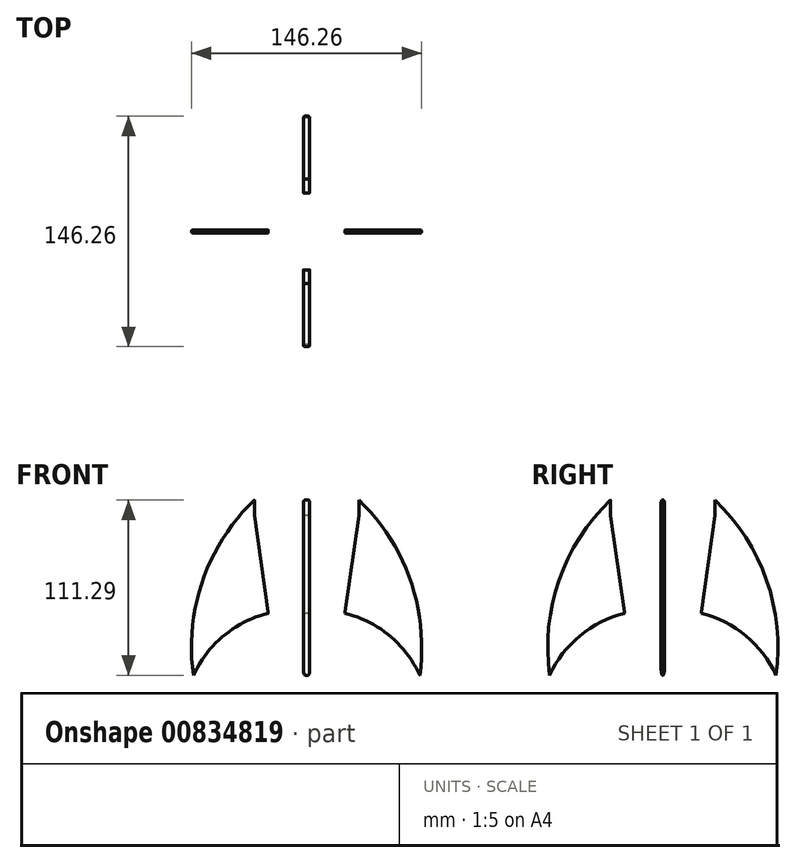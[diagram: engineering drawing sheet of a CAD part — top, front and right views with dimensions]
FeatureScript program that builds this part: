
annotation { "Feature Type Name" : "Feature", "Feature Type Description" : "" }
export const myFeature = defineFeature(function(context is Context, id is Id, definition is map)
    precondition{}
    {
        {
            var Q0;
            Q0=qCreatedBy(makeId("Front.planeOp"),FACE);
            var sketch = newSketch(context, id + "F0", { "sketchPlane" : qUnion([Q0])});
            skLineSegment(sketch, "E0", {"start": v(0, 1.98) * mm, "end": v(0, 124.8) * mm, "construction": true});
            skLineSegment(sketch, "E1.bottom", {"start": v(-9, 31.24) * mm, "end": v(9, 31.24) * mm, "construction": true});
            skLineSegment(sketch, "E1.top", {"start": v(-9, 101.24) * mm, "end": v(9, 101.24) * mm, "construction": true});
            skLineSegment(sketch, "E1.left", {"start": v(-9, 31.24) * mm, "end": v(-9, 101.24) * mm, "construction": true});
            skLineSegment(sketch, "E1.right", {"start": v(9, 31.24) * mm, "end": v(9, 101.24) * mm, "construction": true});
            skSolve(sketch);
        }
        {
            var Q0;
            Q0=qCreatedBy(makeId("Front.planeOp"),FACE);
            var sketch = newSketch(context, id + "F1", { "sketchPlane" : qUnion([Q0])});
            skLineSegment(sketch, "E2.MirrorCS", {"start": v(9.15, 101.26) * mm, "end": v(9.15, 33.17) * mm});
            skLineSegment(sketch, "E3.MirrorCS", {"start": v(33.01, 101.3) * mm, "end": v(23.86, 34.74) * mm});
            skLineSegment(sketch, "E4.MirrorCS", {"start": v(32, 101.3) * mm, "end": v(9.15, 101.26) * mm});
            skLineSegment(sketch, "E5.MirrorCS", {"start": v(32, 101.3) * mm, "end": v(32, 111.3) * mm});
            skLineSegment(sketch, "E6.MirrorCS", {"start": v(33.01, 111.3) * mm, "end": v(33.01, 101.3) * mm});
            skLineSegment(sketch, "E7.MirrorCS", {"start": v(32, 111.3) * mm, "end": v(33.01, 111.3) * mm});
            skLineSegment(sketch, "E8.MirrorCS", {"start": v(19.69, 21.09) * mm, "end": v(19.69, 34.74) * mm});
            skLineSegment(sketch, "E9.MirrorCS", {"start": v(19.69, 34.74) * mm, "end": v(23.86, 34.74) * mm});
            skLineSegment(sketch, "E10.MirrorCS", {"start": v(9.15, 33.17) * mm, "end": v(11.05, 33.17) * mm});
            skLineSegment(sketch, "E11.MirrorCS", {"start": v(11.05, 33.17) * mm, "end": v(11.05, 30.73) * mm});
            skLineSegment(sketch, "E12.MirrorCS", {"start": v(11.05, 30.73) * mm, "end": v(18.59, 21.09) * mm});
            skLineSegment(sketch, "E13.MirrorCS", {"start": v(18.59, 21.09) * mm, "end": v(19.69, 21.09) * mm});
            skLineSegment(sketch, "E14", {"start": v(12.5, 94.18) * mm, "end": v(28.58, 94.18) * mm});
            skLineSegment(sketch, "E15", {"start": v(28.58, 94.18) * mm, "end": v(21.03, 39.29) * mm});
            skLineSegment(sketch, "E16", {"start": v(21.03, 39.29) * mm, "end": v(12.3, 39.29) * mm});
            skLineSegment(sketch, "E17", {"start": v(12.3, 39.29) * mm, "end": v(12.5, 94.18) * mm});
            skSolve(sketch);
        }
        {
            var Q0;
            Q0=sQuery(id+"F1.wireOp",EDGE,"E2.MirrorCS");
            var Q1;
            Q1=sQuery(id+"F1.wireOp",EDGE,"E4.MirrorCS");
            var Q2;
            Q2=sQuery(id+"F1.wireOp",EDGE,"E6.MirrorCS");
            var Q3;
            Q3=sQuery(id+"F1.wireOp",EDGE,"E3.MirrorCS");
            var Q4;
            Q4=sQuery(id+"F1.wireOp",EDGE,"E5.MirrorCS");
            var Q5;
            Q5=sQuery(id+"F1.wireOp",EDGE,"E9.MirrorCS");
            var Q6;
            Q6=sQuery(id+"F1.wireOp",EDGE,"E11.MirrorCS");
            var Q7;
            Q7=sQuery(id+"F1.wireOp",EDGE,"E7.MirrorCS");
            var Q8;
            Q8=sQuery(id+"F1.wireOp",EDGE,"E10.MirrorCS");
            var Q9;
            Q9=sQuery(id+"F1.wireOp",EDGE,"E8.MirrorCS");
            var Q10;
            Q10=sQuery(id+"F1.wireOp",EDGE,"E12.MirrorCS");
            var Q11;
            Q11=sQuery(id+"F1.wireOp",EDGE,"E13.MirrorCS");
            var Q12;
            Q12=sQuery(id+"F0.wireOp",EDGE,"E0");
            revolve(context, id + "F2", {"bodyType" : ToolBodyType.SURFACE, "surfaceOperationType" : NewSurfaceOperationType.NEW, "surfaceEntities" : qUnion([Q0, Q1, Q2, Q3, Q4, Q5, Q6, Q7, Q8, Q9, Q10, Q11]), "axis" : qUnion([Q12]), "revolveType" : RevolveType.FULL});
        }
        {
            var Q0;
            Q0=makeQuery(id+"F2.opRevolve","SWEPT_EDGE",EDGE,{"disambiguationData":[OSD([sQuery(id+"F1.wireOp",VERTEX,"E4.MirrorCS.end")])]});
            var Q1;
            Q1=makeQuery(id+"F2.opRevolve","SWEPT_EDGE",EDGE,{"disambiguationData":[OSD([sQuery(id+"F1.wireOp",VERTEX,"E13.MirrorCS.end")])]});
            var Q2;
            Q2=makeQuery(id+"F2.opRevolve","SWEPT_EDGE",EDGE,{"disambiguationData":[OSD([sQuery(id+"F1.wireOp",VERTEX,"E10.MirrorCS.start")])]});
            fillet(context, id + "F3", {"entities" : qUnion([Q0, Q1, Q2]), "radius" : 5 * mm, "tangentPropagation" : true, "allowEdgeOverflow" : false});
        }
        {
            var Q0;
            Q0=qCreatedBy(makeId("Front.planeOp"),FACE);
            var sketch = newSketch(context, id + "F4", { "sketchPlane" : qUnion([Q0])});
            skArc(sketch, "E18", {"start": v(-24.4, 39.36) * mm, "mid": v(-52.64, 25.1) * mm, "end": v(-71.9, 0) * mm});
            skArc(sketch, "E19", {"start": v(-33.16, 111.3) * mm, "mid": v(-65.94, 60.31) * mm, "end": v(-71.9, 0) * mm});
            skLineSegment(sketch, "E20", {"start": v(-33.16, 111.3) * mm, "end": v(-33.16, 101.44) * mm});
            skLineSegment(sketch, "E21", {"start": v(-33.16, 101.44) * mm, "end": v(-24.4, 39.36) * mm});
            skArc(sketch, "E22.MirrorCS", {"start": v(33.16, 111.3) * mm, "mid": v(65.94, 60.31) * mm, "end": v(71.9, 0) * mm});
            skArc(sketch, "E23.MirrorCS", {"start": v(24.4, 39.36) * mm, "mid": v(52.64, 25.1) * mm, "end": v(71.9, 0) * mm});
            skLineSegment(sketch, "E24.MirrorCS", {"start": v(33.16, 101.44) * mm, "end": v(24.4, 39.36) * mm});
            skLineSegment(sketch, "E25.MirrorCS", {"start": v(33.16, 111.3) * mm, "end": v(33.16, 101.44) * mm});
            skSolve(sketch);
        }
        {
            var Q0;
            Q0 = qSketchRegion(id + "F4", true);
            extrude(context, id + "F5", {"entities" : qUnion([Q0]), "depth" : 1 * mm, "offsetDistance" : 25 * mm, "hasSecondDirection" : true, "secondDirectionOppositeDirection" : true, "secondDirectionDepth" : 1 * mm});
        }
        {
            var Q0;
            Q0=qCreatedBy(makeId("Right.planeOp"),FACE);
            var sketch = newSketch(context, id + "F6", { "sketchPlane" : qUnion([Q0])});
            skArc(sketch, "E26", {"start": v(-24.36, 39.36) * mm, "mid": v(-52.6, 25.1) * mm, "end": v(-71.86, 0) * mm});
            skArc(sketch, "E27", {"start": v(-33.12, 111.3) * mm, "mid": v(-65.9, 60.31) * mm, "end": v(-71.86, 0) * mm});
            skLineSegment(sketch, "E28", {"start": v(-33.12, 111.3) * mm, "end": v(-33.12, 101.44) * mm});
            skLineSegment(sketch, "E29", {"start": v(-33.12, 101.44) * mm, "end": v(-24.36, 39.36) * mm});
            skArc(sketch, "E30.MirrorCS", {"start": v(33.2, 111.3) * mm, "mid": v(65.98, 60.31) * mm, "end": v(71.94, 0) * mm});
            skArc(sketch, "E31.MirrorCS", {"start": v(24.44, 39.36) * mm, "mid": v(52.69, 25.1) * mm, "end": v(71.94, 0) * mm});
            skLineSegment(sketch, "E32.MirrorCS", {"start": v(33.2, 101.44) * mm, "end": v(24.44, 39.36) * mm});
            skLineSegment(sketch, "E33.MirrorCS", {"start": v(33.2, 111.3) * mm, "end": v(33.2, 101.44) * mm});
            skSolve(sketch);
        }
        {
            var Q0;
            Q0 = qSketchRegion(id + "F6", true);
            extrude(context, id + "F7", {"entities" : qUnion([Q0]), "depth" : 2 * mm, "offsetDistance" : 25 * mm, "hasSecondDirection" : true, "secondDirectionOppositeDirection" : true, "secondDirectionDepth" : 2 * mm});
        }
        {
            var Q0;
            Q0=makeQuery(id+"F7.opExtrude","CAP_EDGE",EDGE,{"disambiguationData":[OSD([sQuery(id+"F6.wireOp",EDGE,"E27")])],"isStart":true});
            var Q1;
            Q1=makeQuery(id+"F7.opExtrude","CAP_EDGE",EDGE,{"disambiguationData":[OSD([sQuery(id+"F6.wireOp",EDGE,"E26")])],"isStart":true});
            var Q2;
            Q2=makeQuery(id+"F7.opExtrude","CAP_EDGE",EDGE,{"disambiguationData":[OSD([sQuery(id+"F6.wireOp",EDGE,"E26")])],"isStart":false});
            var Q3;
            Q3=makeQuery(id+"F5.opExtrude","CAP_EDGE",EDGE,{"disambiguationData":[OSD([sQuery(id+"F4.wireOp",EDGE,"E23.MirrorCS")])],"isStart":false});
            var Q4;
            Q4=makeQuery(id+"F5.opExtrude","CAP_EDGE",EDGE,{"disambiguationData":[OSD([sQuery(id+"F4.wireOp",EDGE,"E23.MirrorCS")])],"isStart":true});
            var Q5;
            Q5=makeQuery(id+"F7.opExtrude","CAP_EDGE",EDGE,{"disambiguationData":[OSD([sQuery(id+"F6.wireOp",EDGE,"E31.MirrorCS")])],"isStart":false});
            var Q6;
            Q6=makeQuery(id+"F7.opExtrude","CAP_EDGE",EDGE,{"disambiguationData":[OSD([sQuery(id+"F6.wireOp",EDGE,"E31.MirrorCS")])],"isStart":true});
            var Q7;
            Q7=makeQuery(id+"F5.opExtrude","CAP_EDGE",EDGE,{"disambiguationData":[OSD([sQuery(id+"F4.wireOp",EDGE,"E18")])],"isStart":true});
            var Q8;
            Q8=makeQuery(id+"F5.opExtrude","CAP_EDGE",EDGE,{"disambiguationData":[OSD([sQuery(id+"F4.wireOp",EDGE,"E18")])],"isStart":false});
            var Q9;
            Q9=makeQuery(id+"F5.opExtrude","CAP_EDGE",EDGE,{"disambiguationData":[OSD([sQuery(id+"F4.wireOp",EDGE,"E19")])],"isStart":false});
            var Q10;
            Q10=makeQuery(id+"F5.opExtrude","CAP_EDGE",EDGE,{"disambiguationData":[OSD([sQuery(id+"F4.wireOp",EDGE,"E19")])],"isStart":true});
            var Q11;
            Q11=makeQuery(id+"F7.opExtrude","CAP_EDGE",EDGE,{"disambiguationData":[OSD([sQuery(id+"F6.wireOp",EDGE,"E27")])],"isStart":false});
            var Q12;
            Q12=makeQuery(id+"F5.opExtrude","CAP_EDGE",EDGE,{"disambiguationData":[OSD([sQuery(id+"F4.wireOp",EDGE,"E22.MirrorCS")])],"isStart":true});
            var Q13;
            Q13=makeQuery(id+"F5.opExtrude","CAP_EDGE",EDGE,{"disambiguationData":[OSD([sQuery(id+"F4.wireOp",EDGE,"E22.MirrorCS")])],"isStart":false});
            var Q14;
            Q14=makeQuery(id+"F7.opExtrude","CAP_EDGE",EDGE,{"disambiguationData":[OSD([sQuery(id+"F6.wireOp",EDGE,"E30.MirrorCS")])],"isStart":true});
            var Q15;
            Q15=makeQuery(id+"F7.opExtrude","CAP_EDGE",EDGE,{"disambiguationData":[OSD([sQuery(id+"F6.wireOp",EDGE,"E30.MirrorCS")])],"isStart":false});
            fillet(context, id + "F8", {"entities" : qUnion([Q0, Q1, Q2, Q3, Q4, Q5, Q6, Q7, Q8, Q9, Q10, Q11, Q12, Q13, Q14, Q15]), "radius" : 1 * mm, "tangentPropagation" : true, "allowEdgeOverflow" : false});
        }
    });
